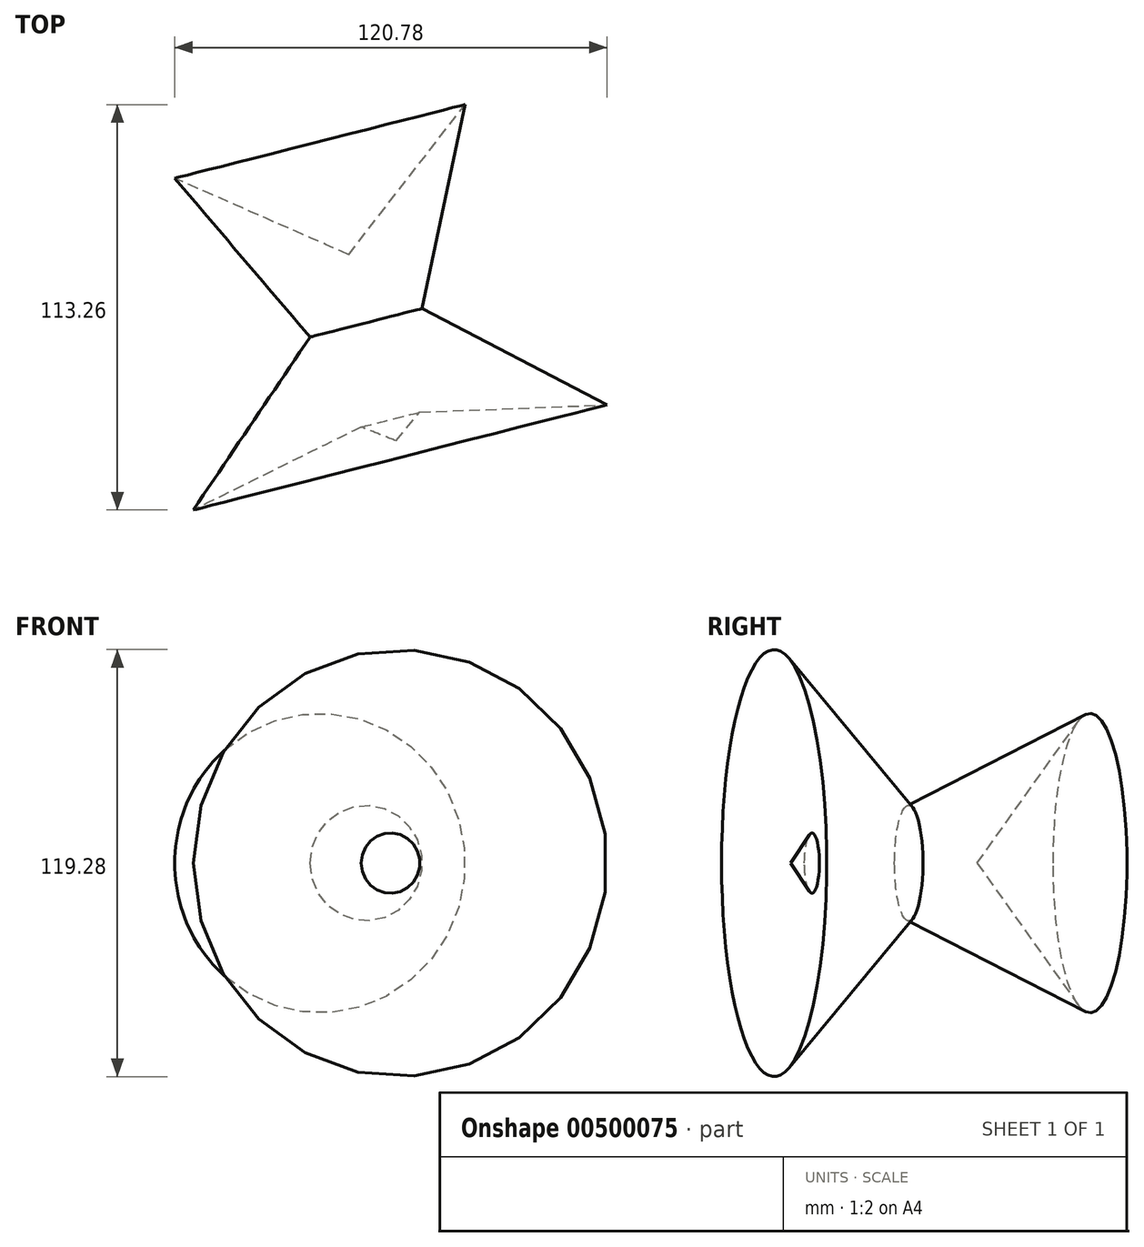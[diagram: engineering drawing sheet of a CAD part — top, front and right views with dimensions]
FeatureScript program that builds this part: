
annotation { "Feature Type Name" : "Feature", "Feature Type Description" : "" }
export const myFeature = defineFeature(function(context is Context, id is Id, definition is map)
    precondition{}
    {
        {
            var Q0;
            Q0=qCreatedBy(makeId("Top.planeOp"),FACE);
            var sketch = newSketch(context, id + "F0", { "sketchPlane" : qUnion([Q0])});
            skLineSegment(sketch, "E0", {"start": v(0, 21.49) * mm, "end": v(42.67, 48) * mm});
            skLineSegment(sketch, "E1", {"start": v(42.67, 48) * mm, "end": v(28.65, 0) * mm});
            skLineSegment(sketch, "E2", {"start": v(28.65, 0) * mm, "end": v(58.52, -48.31) * mm});
            skLineSegment(sketch, "E3", {"start": v(58.52, -48.31) * mm, "end": v(0, -25.15) * mm});
            skLineSegment(sketch, "E4", {"start": v(0, -25.15) * mm, "end": v(-46.94, -48.31) * mm});
            skLineSegment(sketch, "E5", {"start": v(-46.94, -48.31) * mm, "end": v(-14.33, 0) * mm});
            skLineSegment(sketch, "E6", {"start": v(-14.33, 0) * mm, "end": v(-52.12, 44.35) * mm});
            skLineSegment(sketch, "E7", {"start": v(-52.12, 44.35) * mm, "end": v(0, 21.49) * mm});
            skLineSegment(sketch, "E8", {"start": v(-14.5, 66.18) * mm, "end": v(28.3, -102.3) * mm});
            skSolve(sketch);
        }
        {
            var Q0;
            {var subQ1=sQuery(id+"F0.wireOp",EDGE,"E4");Q0=makeQuery(id+"F0.imprint","IMPRINT",FACE,{"disambiguationData":[TD([[makeQuery(id+"F0.imprint","IMPRINT",EDGE,{"derivedFrom":subQ1}),-1.0]])]});}
            var Q1;
            Q1=sQuery(id+"F0.wireOp",EDGE,"E8");
            revolve(context, id + "F1", {"entities" : qUnion([Q0]), "axis" : qUnion([Q1]), "revolveType" : RevolveType.FULL});
        }
    });
